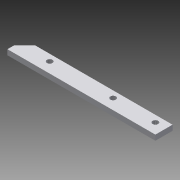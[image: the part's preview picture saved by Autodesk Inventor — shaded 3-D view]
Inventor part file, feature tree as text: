
AUTODESK INVENTOR PART (.ipt)
format: ipt  version: 2015 (Build 190159000, 159)  size: 99,328 bytes
history: native  units: in
note: dims shown in document units (in); Inventor stores cm internally (conversion verified against a paired STEP export)
features: extrude x1, sketch x1
ambient origin geometry x8: Origin, YZ Plane, XZ Plane, XY Plane, X Axis, Y Axis, Z Axis, Center Point
bodies: Solid1 (feature_tree)
feature tree (2):
  extrude  "Extrusion1"  Depth=0.8125in
  sketch  "Sketch1"  dims[d0=7.0in d1=0.8125in d2=0.5in d3=0.5in d4=0.5in d5=0.5in d6=0.5in d7=0.5in d8=2.5in d9=5.5in d10=0.2656in d11=0.2656in d12=0.2656in d13=0.25in d14=0.0in]
